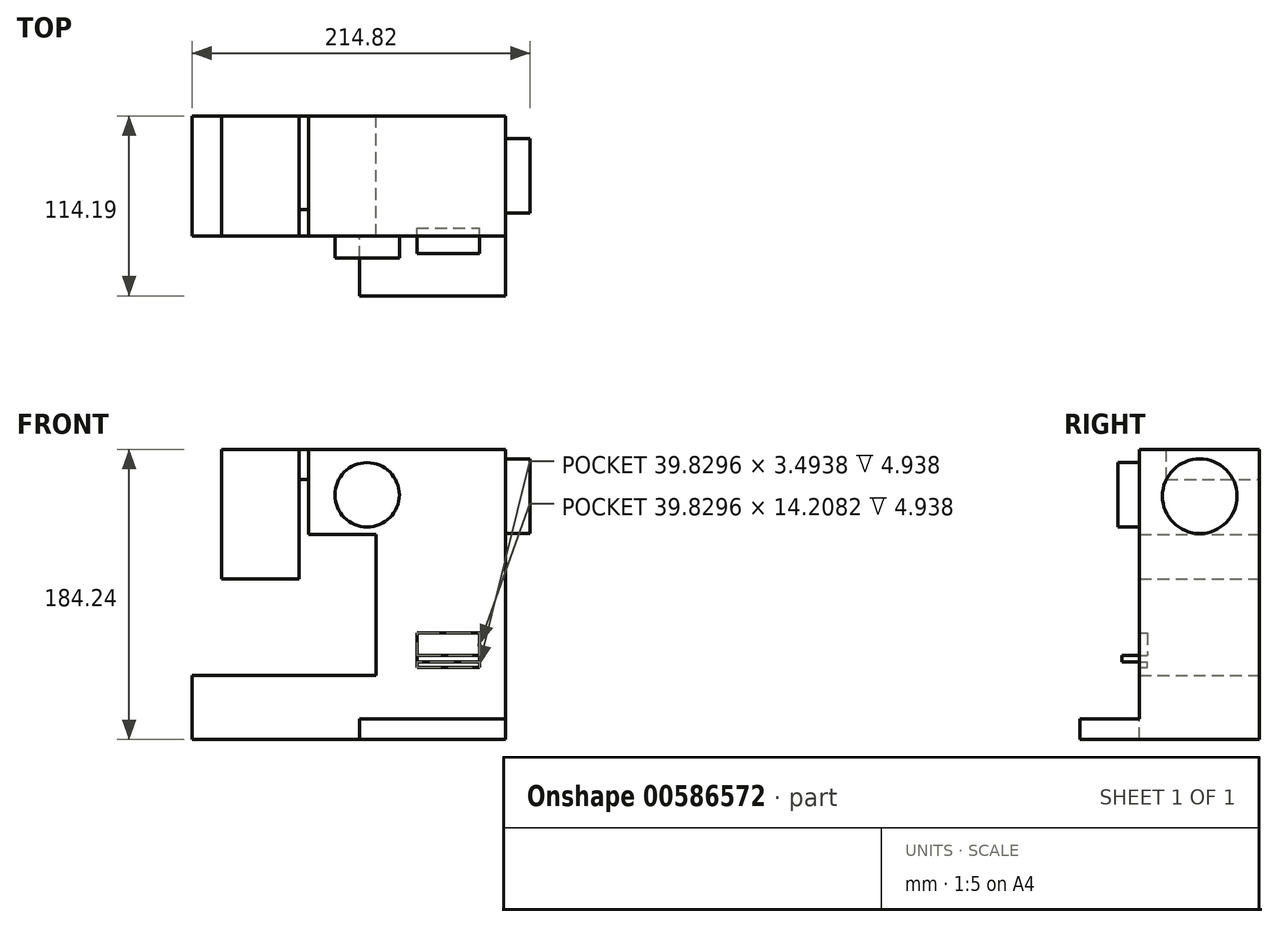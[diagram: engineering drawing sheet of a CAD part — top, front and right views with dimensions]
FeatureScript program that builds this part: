
annotation { "Feature Type Name" : "Feature", "Feature Type Description" : "" }
export const myFeature = defineFeature(function(context is Context, id is Id, definition is map)
    precondition{}
    {
        {
            var Q0;
            Q0=qCreatedBy(makeId("Front.planeOp"),FACE);
            var sketch = newSketch(context, id + "F0", { "sketchPlane" : qUnion([Q0])});
            skLineSegment(sketch, "E0", {"start": v(-73.25, 5.39) * mm, "end": v(-23.9, 5.39) * mm});
            skLineSegment(sketch, "E1", {"start": v(-23.9, 5.39) * mm, "end": v(-23.9, 33.58) * mm});
            skLineSegment(sketch, "E2", {"start": v(-23.9, 33.58) * mm, "end": v(24.87, 33.58) * mm});
            skLineSegment(sketch, "E3", {"start": v(24.87, 33.58) * mm, "end": v(24.87, -56.11) * mm});
            skLineSegment(sketch, "E4", {"start": v(24.87, -56.11) * mm, "end": v(-92.06, -56.11) * mm});
            skLineSegment(sketch, "E5", {"start": v(-92.06, -56.11) * mm, "end": v(-92.06, -96.65) * mm});
            skLineSegment(sketch, "E6", {"start": v(-92.06, -96.65) * mm, "end": v(14.51, -96.65) * mm});
            skLineSegment(sketch, "E7", {"start": v(14.51, -96.65) * mm, "end": v(14.51, -83.6) * mm});
            skLineSegment(sketch, "E8", {"start": v(14.51, -83.6) * mm, "end": v(107.21, -83.6) * mm});
            skLineSegment(sketch, "E9", {"start": v(107.21, -83.6) * mm, "end": v(107.21, -96.65) * mm});
            skLineSegment(sketch, "E10", {"start": v(107.21, -96.65) * mm, "end": v(14.51, -96.65) * mm});
            skLineSegment(sketch, "E11", {"start": v(107.21, -83.6) * mm, "end": v(107.21, 87.59) * mm});
            skLineSegment(sketch, "E12", {"start": v(107.21, 87.59) * mm, "end": v(-73.25, 87.59) * mm});
            skLineSegment(sketch, "E13", {"start": v(-73.25, 87.59) * mm, "end": v(-73.25, 5.39) * mm});
            skCircle(sketch, "E14", {"center": v(19.17, 58.7) * mm, "radius": 20.47 * mm});
            skLineSegment(sketch, "E15", {"start": v(50.85, -51) * mm, "end": v(90.68, -51) * mm});
            skLineSegment(sketch, "E16", {"start": v(90.68, -51) * mm, "end": v(90.68, -29.1) * mm});
            skLineSegment(sketch, "E17", {"start": v(50.85, -43.31) * mm, "end": v(90.68, -43.31) * mm});
            skLineSegment(sketch, "E18", {"start": v(90.68, -43.31) * mm, "end": v(90.68, -47.5) * mm});
            skLineSegment(sketch, "E19", {"start": v(90.68, -47.5) * mm, "end": v(50.85, -47.5) * mm});
            skLineSegment(sketch, "E20", {"start": v(50.85, -47.5) * mm, "end": v(50.85, -43.31) * mm});
            skLineSegment(sketch, "E21", {"start": v(90.68, -29.1) * mm, "end": v(50.85, -29.1) * mm});
            skLineSegment(sketch, "E22", {"start": v(50.85, -29.1) * mm, "end": v(50.85, -51) * mm});
            skLineSegment(sketch, "E23", {"start": v(-23.91, 87.59) * mm, "end": v(-23.91, 33.58) * mm});
            skLineSegment(sketch, "E24", {"start": v(-23.91, 33.58) * mm, "end": v(-18.03, 33.58) * mm});
            skLineSegment(sketch, "E25", {"start": v(-18.03, 33.58) * mm, "end": v(-18.03, 87.59) * mm});
            skLineSegment(sketch, "E26", {"start": v(-18.03, 87.59) * mm, "end": v(-23.91, 87.59) * mm});
            skLineSegment(sketch, "E27", {"start": v(-23.91, 68.5) * mm, "end": v(-18.03, 68.5) * mm});
            skLineSegment(sketch, "E28", {"start": v(24.87, 58.7) * mm, "end": v(19.17, 58.7) * mm});
            skLineSegment(sketch, "E29", {"start": v(24.87, 33.58) * mm, "end": v(24.87, 58.7) * mm});
            skSolve(sketch);
        }
        {
            var Q0;
            Q0=qCreatedBy(makeId("Right.planeOp"),FACE);
            var sketch = newSketch(context, id + "F1", { "sketchPlane" : qUnion([Q0])});
            skCircle(sketch, "E30", {"center": v(-37.94, 57.86) * mm, "radius": 23.72 * mm});
            skSolve(sketch);
        }
        {
            var Q0;
            Q0=makeQuery(id+"F0.imprint","IMPRINT",FACE,{"disambiguationData":[TD([[makeQuery(id+"F0.imprint","IMPRINT",EDGE,{"derivedFrom":sQuery(id+"F0.wireOp",EDGE,"E0")}),1.0]])]});
            var Q1;
            {var subQ0=sQuery(id+"F0.wireOp",EDGE,"E3");Q1=makeQuery(id+"F0.imprint","IMPRINT",FACE,{"disambiguationData":[TD([[makeQuery(id+"F0.imprint","IMPRINT",EDGE,{"derivedFrom":subQ0}),1.0]])]});}
            extrude(context, id + "F2", {"entities" : qUnion([Q0, Q1]), "depth" : 76.2 * mm, "offsetDistance" : 25.4 * mm});
        }
        {
            var Q0;
            Q0=makeQuery(id+"F0.imprint","IMPRINT",FACE,{"disambiguationData":[TD([[makeQuery(id+"F0.imprint","IMPRINT",EDGE,{"derivedFrom":sQuery(id+"F0.wireOp",EDGE,"E14")}),1.0]])]});
            extrude(context, id + "F3", {"entities" : qUnion([Q0]), "operationType" : NewBodyOperationType.ADD, "depth" : 90.03 * mm, "offsetDistance" : 25.4 * mm});
        }
        {
            var Q0;
            {var subQ2=sQuery(id+"F0.wireOp",EDGE,"E17");Q0=makeQuery(id+"F0.imprint","IMPRINT",FACE,{"disambiguationData":[TD([[makeQuery(id+"F0.imprint","IMPRINT",EDGE,{"derivedFrom":subQ2}),1.0]])]});}
            var Q1;
            {var subQ0=sQuery(id+"F0.wireOp",EDGE,"E15");Q1=makeQuery(id+"F0.imprint","IMPRINT",FACE,{"disambiguationData":[TD([[makeQuery(id+"F0.imprint","IMPRINT",EDGE,{"derivedFrom":subQ0}),1.0]])]});}
            extrude(context, id + "F4", {"entities" : qUnion([Q0, Q1]), "operationType" : NewBodyOperationType.ADD, "depth" : 71.26 * mm, "offsetDistance" : 25.4 * mm});
        }
        {
            var Q0;
            {var subQ0=sQuery(id+"F0.wireOp",EDGE,"E17");Q0=makeQuery(id+"F0.imprint","IMPRINT",FACE,{"disambiguationData":[TD([[makeQuery(id+"F0.imprint","IMPRINT",EDGE,{"derivedFrom":subQ0}),-1.0]])]});}
            extrude(context, id + "F5", {"entities" : qUnion([Q0]), "operationType" : NewBodyOperationType.ADD, "depth" : 87.28 * mm, "offsetDistance" : 25.4 * mm});
        }
        {
            var Q0;
            Q0=makeQuery(id+"F0.imprint","IMPRINT",FACE,{"disambiguationData":[TD([[makeQuery(id+"F0.imprint","IMPRINT",EDGE,{"derivedFrom":sQuery(id+"F0.wireOp",EDGE,"E7")}),-1.0]])]});
            extrude(context, id + "F6", {"entities" : qUnion([Q0]), "operationType" : NewBodyOperationType.ADD, "depth" : 114.19 * mm, "offsetDistance" : 25.4 * mm});
        }
        {
            var Q0;
            Q0=makeQuery(id+"F0.imprint","IMPRINT",FACE,{"disambiguationData":[TD([[makeQuery(id+"F0.imprint","IMPRINT",EDGE,{"derivedFrom":sQuery(id+"F0.wireOp",EDGE,"E23")}),1.0]])]});
            extrude(context, id + "F7", {"entities" : qUnion([Q0]), "depth" : 59.22 * mm});
        }
        {
            var Q0;
            Q0=qSketchRegion(id+"F1",true);
            extrude(context, id + "F8", {"entities" : qUnion([Q0]), "operationType" : NewBodyOperationType.ADD, "depth" : 122.76 * mm});
        }
    });
